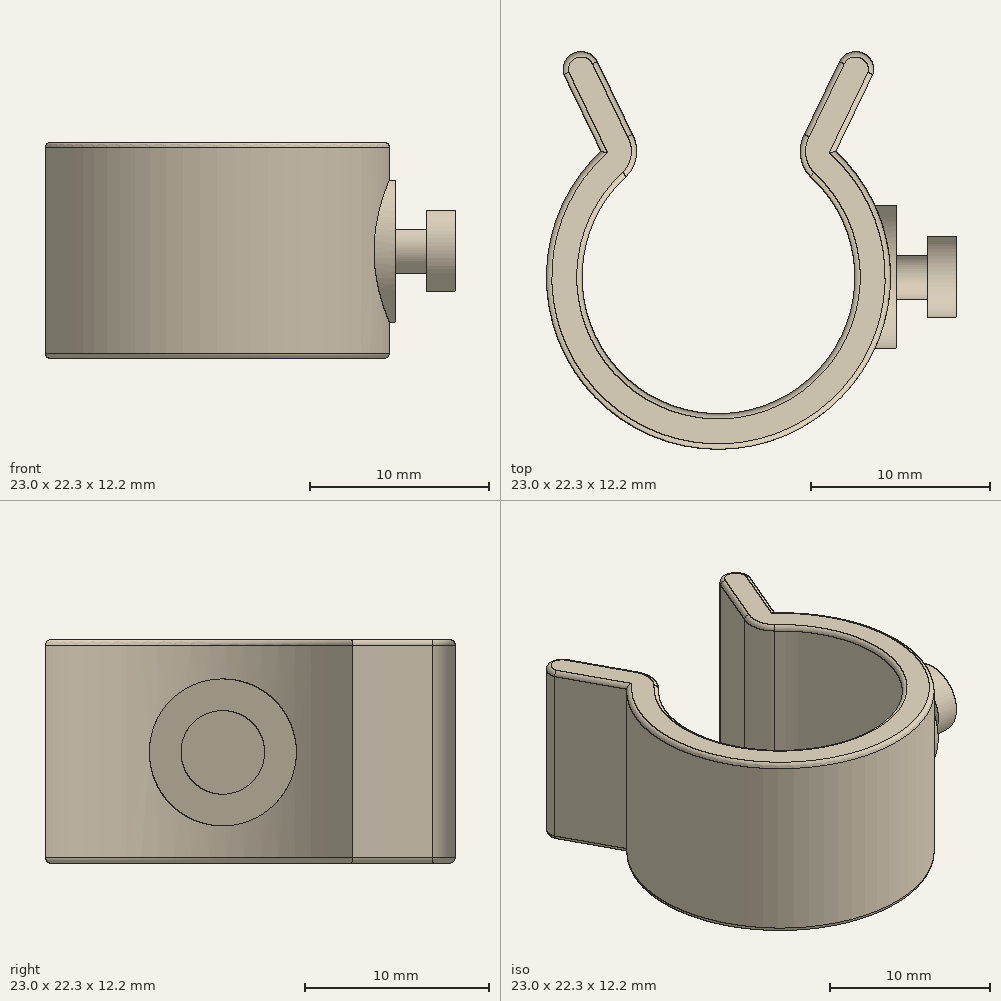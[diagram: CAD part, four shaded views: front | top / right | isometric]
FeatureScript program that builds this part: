
annotation { "Feature Type Name" : "Feature", "Feature Type Description" : "" }
export const myFeature = defineFeature(function(context is Context, id is Id, definition is map)
    precondition{}
    {
        {
            var Q0;
            Q0=qCreatedBy(makeId("Top.planeOp"),FACE);
            var sketch = newSketch(context, id + "F0", { "sketchPlane" : qUnion([Q0])});
            skArc(sketch, "E0", {"start": v(-5.16, 5.65) * mm, "mid": v(0, -7.65) * mm, "end": v(5.16, 5.65) * mm});
            skArc(sketch, "E1", {"start": v(-6.59, 7.05) * mm, "mid": v(0.01, -9.65) * mm, "end": v(6.57, 7.07) * mm});
            skLineSegment(sketch, "E2", {"start": v(7.65, 0) * mm, "end": v(9.65, 0) * mm, "construction": true});
            skArc(sketch, "E3", {"start": v(-5.16, 5.65) * mm, "mid": v(-4.6, 6.77) * mm, "end": v(-4.83, 8) * mm});
            skLineSegment(sketch, "E4", {"start": v(-6.59, 7.05) * mm, "end": v(-8.67, 11.38) * mm});
            skLineSegment(sketch, "E5", {"start": v(-4.83, 8) * mm, "end": v(-6.8, 12.09) * mm});
            skLineSegment(sketch, "E6.MirrorCS", {"start": v(4.83, 8) * mm, "end": v(6.8, 12.09) * mm});
            skLineSegment(sketch, "E7.MirrorCS", {"start": v(6.59, 7.05) * mm, "end": v(8.67, 11.38) * mm});
            skArc(sketch, "E8.MirrorCS", {"start": v(5.16, 5.65) * mm, "mid": v(4.6, 6.77) * mm, "end": v(4.83, 8) * mm});
            skLineSegment(sketch, "E9", {"start": v(-7.7, 11.65) * mm, "end": v(7.7, 11.65) * mm, "construction": true});
            skArc(sketch, "E10", {"start": v(-6.8, 12.09) * mm, "mid": v(-8.06, 12.6) * mm, "end": v(-8.67, 11.38) * mm});
            skArc(sketch, "E11.MirrorCS", {"start": v(6.8, 12.09) * mm, "mid": v(8.06, 12.6) * mm, "end": v(8.67, 11.38) * mm});
            skLineSegment(sketch, "E12", {"start": v(-4.6, 6.8) * mm, "end": v(4.6, 6.8) * mm, "construction": true});
            skSolve(sketch);
        }
        {
            var Q0;
            Q0=qSketchRegion(id+"F0",true);
            extrude(context, id + "F1", {"entities" : qUnion([Q0]), "depth" : 12.15 * mm});
        }
        {
            var Q0;
            Q0=qCreatedBy(makeId("Right.planeOp"),FACE);
            cPlane(context, id + "F2", {"entities" : qUnion([Q0]), "cplaneType" : CPlaneType.OFFSET, "offset" : 8 * mm, "width" : 150 * mm, "height" : 150 * mm});
        }
        {
            var Q0;
            Q0=qCreatedBy(id+"F2.planeOp",FACE);
            var sketch = newSketch(context, id + "F3", { "sketchPlane" : qUnion([Q0])});
            skCircle(sketch, "E13", {"center": v(0, 6.02) * mm, "radius": 4 * mm});
            skCircle(sketch, "E14", {"center": v(0, 6.02) * mm, "radius": 1.25 * mm});
            skSolve(sketch);
        }
        {
            var Q0;
            Q0=qSketchRegion(id+"F3",true);
            extrude(context, id + "F4", {"entities" : qUnion([Q0]), "operationType" : NewBodyOperationType.ADD, "depth" : 2 * mm});
        }
        {
            var Q0;
            Q0=makeQuery(id+"F3.imprint","IMPRINT",FACE,{"disambiguationData":[TD([[makeQuery(id+"F3.imprint","IMPRINT",EDGE,{"derivedFrom":sQuery(id+"F3.wireOp",EDGE,"E14")}),1.0]])]});
            var Q1;
            Q1=sQuery(id+"F3.wireOp",EDGE,"E14");
            extrude(context, id + "F5", {"entities" : qUnion([Q0]), "operationType" : NewBodyOperationType.ADD, "surfaceEntities" : qUnion([Q1]), "depth" : 3.75 * mm});
        }
        {
            var Q0;
            Q0=qCreatedBy(makeId("Right.planeOp"),FACE);
            cPlane(context, id + "F6", {"entities" : qUnion([Q0]), "cplaneType" : CPlaneType.OFFSET, "offset" : 11.75 * mm, "width" : 150 * mm, "height" : 150 * mm});
        }
        {
            var Q0;
            Q0=qCreatedBy(id+"F6.planeOp",FACE);
            var sketch = newSketch(context, id + "F7", { "sketchPlane" : qUnion([Q0])});
            skCircle(sketch, "E15", {"center": v(0, 6.02) * mm, "radius": 2.27 * mm});
            skSolve(sketch);
        }
        {
            var Q0;
            Q0=makeQuery(id+"F7.imprint","IMPRINT",FACE,{"disambiguationData":[TD([[makeQuery(id+"F7.imprint","IMPRINT",EDGE,{"derivedFrom":sQuery(id+"F7.wireOp",EDGE,"E15")}),1.0]])]});
            var Q1;
            Q1=sQuery(id+"F7.wireOp",EDGE,"E15");
            extrude(context, id + "F8", {"entities" : qUnion([Q0]), "operationType" : NewBodyOperationType.ADD, "surfaceEntities" : qUnion([Q1]), "depth" : 1.6 * mm});
        }
        {
            var Q0;
            Q0=makeQuery(id+"F1.opExtrude","CAP_EDGE",EDGE,{"disambiguationData":[OSD([sQuery(id+"F0.wireOp",EDGE,"E1")])],"isStart":false});
            var Q1;
            Q1=makeQuery(id+"F1.opExtrude","CAP_EDGE",EDGE,{"disambiguationData":[OSD([sQuery(id+"F0.wireOp",EDGE,"E4")])],"isStart":false});
            var Q2;
            Q2=makeQuery(id+"F1.opExtrude","CAP_EDGE",EDGE,{"disambiguationData":[OSD([sQuery(id+"F0.wireOp",EDGE,"E10")])],"isStart":false});
            var Q3;
            Q3=makeQuery(id+"F1.opExtrude","CAP_EDGE",EDGE,{"disambiguationData":[OSD([sQuery(id+"F0.wireOp",EDGE,"E5")])],"isStart":false});
            var Q4;
            Q4=makeQuery(id+"F1.opExtrude","CAP_EDGE",EDGE,{"disambiguationData":[OSD([sQuery(id+"F0.wireOp",EDGE,"E3")])],"isStart":false});
            var Q5;
            Q5=makeQuery(id+"F1.opExtrude","CAP_EDGE",EDGE,{"disambiguationData":[OSD([sQuery(id+"F0.wireOp",EDGE,"E0")])],"isStart":false});
            var Q6;
            Q6=makeQuery(id+"F1.opExtrude","CAP_EDGE",EDGE,{"disambiguationData":[OSD([sQuery(id+"F0.wireOp",EDGE,"E8.MirrorCS")])],"isStart":false});
            var Q7;
            Q7=makeQuery(id+"F1.opExtrude","CAP_EDGE",EDGE,{"disambiguationData":[OSD([sQuery(id+"F0.wireOp",EDGE,"E6.MirrorCS")])],"isStart":false});
            var Q8;
            Q8=makeQuery(id+"F1.opExtrude","CAP_EDGE",EDGE,{"disambiguationData":[OSD([sQuery(id+"F0.wireOp",EDGE,"E11.MirrorCS")])],"isStart":false});
            var Q9;
            Q9=makeQuery(id+"F1.opExtrude","CAP_EDGE",EDGE,{"disambiguationData":[OSD([sQuery(id+"F0.wireOp",EDGE,"E7.MirrorCS")])],"isStart":false});
            fillet(context, id + "F9", {"entities" : qUnion([Q0, Q1, Q2, Q3, Q4, Q5, Q6, Q7, Q8, Q9]), "radius" : 0.3 * mm, "tangentPropagation" : true, "allowEdgeOverflow" : false});
        }
        {
            var Q0;
            Q0=makeQuery(id+"F1.opExtrude","CAP_EDGE",EDGE,{"disambiguationData":[OSD([sQuery(id+"F0.wireOp",EDGE,"E7.MirrorCS")])],"isStart":true});
            var Q1;
            Q1=makeQuery(id+"F1.opExtrude","CAP_EDGE",EDGE,{"disambiguationData":[OSD([sQuery(id+"F0.wireOp",EDGE,"E11.MirrorCS")])],"isStart":true});
            var Q2;
            Q2=makeQuery(id+"F1.opExtrude","CAP_EDGE",EDGE,{"disambiguationData":[OSD([sQuery(id+"F0.wireOp",EDGE,"E6.MirrorCS")])],"isStart":true});
            var Q3;
            Q3=makeQuery(id+"F1.opExtrude","CAP_EDGE",EDGE,{"disambiguationData":[OSD([sQuery(id+"F0.wireOp",EDGE,"E8.MirrorCS")])],"isStart":true});
            var Q4;
            Q4=makeQuery(id+"F1.opExtrude","CAP_EDGE",EDGE,{"disambiguationData":[OSD([sQuery(id+"F0.wireOp",EDGE,"E0")])],"isStart":true});
            var Q5;
            Q5=makeQuery(id+"F1.opExtrude","CAP_EDGE",EDGE,{"disambiguationData":[OSD([sQuery(id+"F0.wireOp",EDGE,"E3")])],"isStart":true});
            var Q6;
            Q6=makeQuery(id+"F1.opExtrude","CAP_EDGE",EDGE,{"disambiguationData":[OSD([sQuery(id+"F0.wireOp",EDGE,"E5")])],"isStart":true});
            var Q7;
            Q7=makeQuery(id+"F1.opExtrude","CAP_EDGE",EDGE,{"disambiguationData":[OSD([sQuery(id+"F0.wireOp",EDGE,"E10")])],"isStart":true});
            var Q8;
            Q8=makeQuery(id+"F1.opExtrude","CAP_EDGE",EDGE,{"disambiguationData":[OSD([sQuery(id+"F0.wireOp",EDGE,"E4")])],"isStart":true});
            var Q9;
            Q9=makeQuery(id+"F1.opExtrude","CAP_EDGE",EDGE,{"disambiguationData":[OSD([sQuery(id+"F0.wireOp",EDGE,"E1")])],"isStart":true});
            fillet(context, id + "F10", {"entities" : qUnion([Q0, Q1, Q2, Q3, Q4, Q5, Q6, Q7, Q8, Q9]), "radius" : 0.3 * mm, "tangentPropagation" : true, "allowEdgeOverflow" : false});
        }
    });
